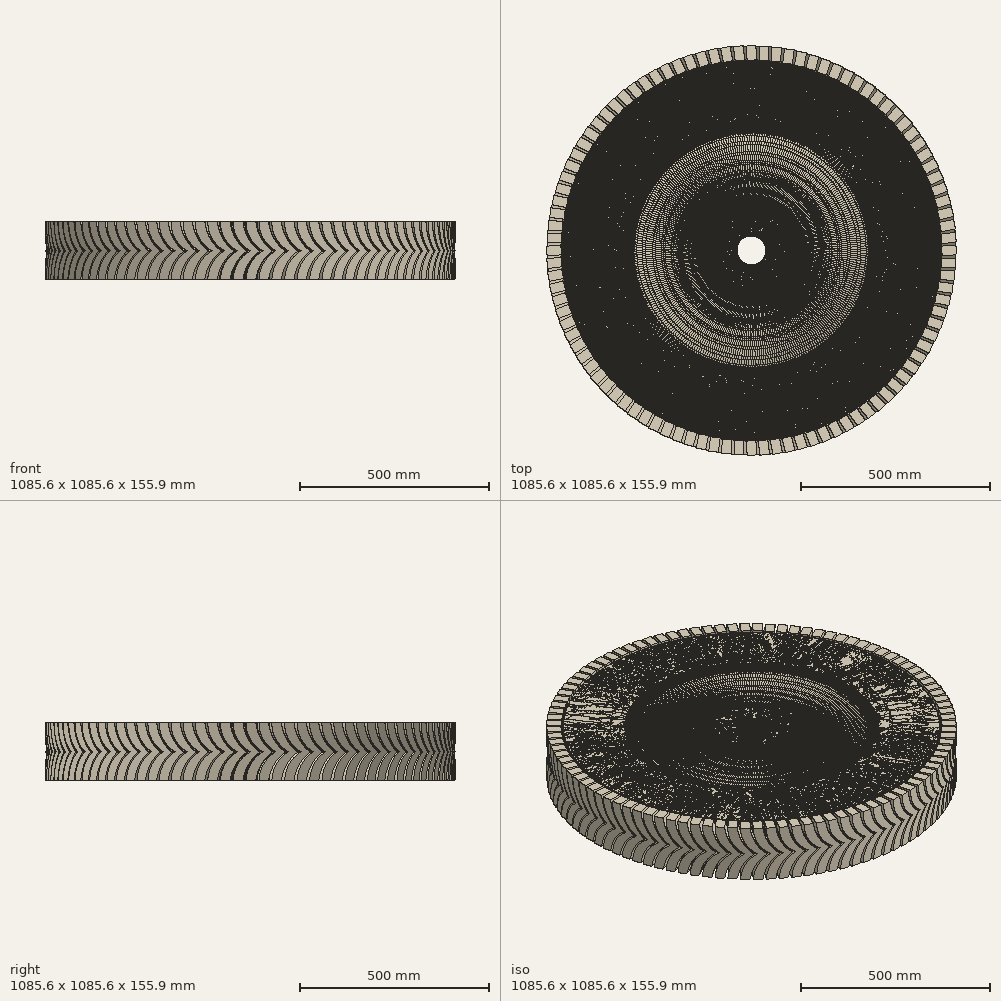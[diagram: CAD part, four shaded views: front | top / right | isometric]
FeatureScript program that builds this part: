
annotation { "Feature Type Name" : "Feature", "Feature Type Description" : "" }
export const myFeature = defineFeature(function(context is Context, id is Id, definition is map)
    precondition{}
    {
        {
            var Q0;
            Q0=qCreatedBy(makeId("Front.planeOp"),FACE);
            var sketch = newSketch(context, id + "F0", { "sketchPlane" : qUnion([Q0])});
            skLineSegment(sketch, "E0", {"start": v(0, 0) * mm, "end": v(0, -107.13) * mm, "construction": true});
            skLineSegment(sketch, "E1", {"start": v(0, 0) * mm, "end": v(0, 107.06) * mm, "construction": true});
            skLineSegment(sketch, "E2", {"start": v(0, 78.3) * mm, "end": v(0, -74.1) * mm});
            skLineSegment(sketch, "E3", {"start": v(0, -74.1) * mm, "end": v(101.6, -74.1) * mm});
            skLineSegment(sketch, "E4", {"start": v(0, 78.3) * mm, "end": v(101.6, 78.3) * mm});
            skLineSegment(sketch, "E5", {"start": v(0, 0) * mm, "end": v(373.98, 0) * mm, "construction": true});
            skArc(sketch, "E6", {"start": v(101.6, 78.3) * mm, "mid": v(218.74, 49.67) * mm, "end": v(335.88, 78.3) * mm});
            skArc(sketch, "E7", {"start": v(335.88, -74.1) * mm, "mid": v(218.74, -45.48) * mm, "end": v(101.6, -74.1) * mm});
            skLineSegment(sketch, "E8", {"start": v(335.88, 78.3) * mm, "end": v(373.98, 78.3) * mm});
            skLineSegment(sketch, "E9", {"start": v(373.98, 78.3) * mm, "end": v(373.98, 65.6) * mm});
            skLineSegment(sketch, "E10", {"start": v(373.98, 65.6) * mm, "end": v(348.58, 65.6) * mm});
            skLineSegment(sketch, "E11", {"start": v(335.88, -74.1) * mm, "end": v(373.98, -74.1) * mm});
            skLineSegment(sketch, "E12", {"start": v(373.98, -74.1) * mm, "end": v(373.98, -61.4) * mm});
            skLineSegment(sketch, "E13", {"start": v(373.98, -61.4) * mm, "end": v(348.58, -61.4) * mm});
            skLineSegment(sketch, "E14", {"start": v(348.58, 65.6) * mm, "end": v(348.58, -61.4) * mm});
            skSolve(sketch);
        }
        {
            var Q0;
            Q0=makeQuery(id+"F0.imprint","IMPRINT",FACE,{"disambiguationData":[TD([[makeQuery(id+"F0.imprint","IMPRINT",EDGE,{"derivedFrom":sQuery(id+"F0.wireOp",EDGE,"E2")}),1.0]])]});
            var Q1;
            Q1=sQuery(id+"F0.wireOp",EDGE,"E1");
            revolve(context, id + "F1", {"entities" : qUnion([Q0]), "axis" : qUnion([Q1]), "revolveType" : RevolveType.FULL});
        }
        {
            var Q0;
            Q0=qCreatedBy(makeId("Top.planeOp"),FACE);
            var sketch = newSketch(context, id + "F2", { "sketchPlane" : qUnion([Q0])});
            skArc(sketch, "E15", {"start": v(-132.61, -265.07) * mm, "mid": v(136.67, -263) * mm, "end": v(293.13, -43.83) * mm});
            skLineSegment(sketch, "E16", {"start": v(0, 0) * mm, "end": v(491.38, -8.3) * mm, "construction": true});
            skArc(sketch, "E17", {"start": v(293.13, -43.83) * mm, "mid": v(196.1, -23.66) * mm, "end": v(97.19, -29.53) * mm});
            skArc(sketch, "E18.2.0", {"start": v(-29.3, -97.26) * mm, "mid": v(-86.9, -177.5) * mm, "end": v(-132.61, -265.07) * mm});
            skArc(sketch, "E19.1.0", {"start": v(98.87, 23.26) * mm, "mid": v(197.17, 13.5) * mm, "end": v(295.86, 17.69) * mm});
            skArc(sketch, "E19.1.1", {"start": v(-108.6, 275.77) * mm, "mid": v(-77.56, 181.67) * mm, "end": v(-23.02, 98.93) * mm});
            skArc(sketch, "E19.2.0", {"start": v(-69.58, 74) * mm, "mid": v(-110.27, 164) * mm, "end": v(-163.25, 247.38) * mm});
            skArc(sketch, "E19.2.1", {"start": v(-184.52, -231.94) * mm, "mid": v(-118.55, -158) * mm, "end": v(-74.16, -69.4) * mm});
            skArc(sketch, "E20.trimOffspring", {"start": v(-69.58, 74) * mm, "mid": v(-101.52, 3.24) * mm, "end": v(-74.16, -69.4) * mm});
            skArc(sketch, "E21.trimOffspring", {"start": v(-163.25, 247.38) * mm, "mid": v(-296.1, 13.14) * mm, "end": v(-184.52, -231.94) * mm});
            skArc(sketch, "E22.trimOffspring", {"start": v(98.87, 23.26) * mm, "mid": v(53.57, 86.3) * mm, "end": v(-23.02, 98.93) * mm});
            skArc(sketch, "E23.trimOffspring", {"start": v(295.86, 17.69) * mm, "mid": v(159.43, 249.86) * mm, "end": v(-108.6, 275.77) * mm});
            skArc(sketch, "E24", {"start": v(-29.3, -97.26) * mm, "mid": v(47.84, -89.33) * mm, "end": v(97.19, -29.53) * mm});
            skSolve(sketch);
        }
        {
            var Q0;
            Q0 = qSketchRegion(id + "F2", true);
            extrude(context, id + "F3", {"entities" : qUnion([Q0]), "operationType" : NewBodyOperationType.REMOVE, "endBound" : BoundingType.SYMMETRIC, "oppositeDirection" : true, "depth" : 553.72 * mm});
        }
        {
            var Q0;
            Q0=qCreatedBy(makeId("Top.planeOp"),FACE);
            var sketch = newSketch(context, id + "F4", { "sketchPlane" : qUnion([Q0])});
            skCircle(sketch, "E25", {"center": v(0, 0) * mm, "radius": 38.1 * mm});
            skCircle(sketch, "E26", {"center": v(11.35, 73) * mm, "radius": 19.05 * mm});
            skCircle(sketch, "E27.1.0", {"center": v(-68.89, -26.67) * mm, "radius": 19.05 * mm});
            skCircle(sketch, "E27.2.0", {"center": v(57.54, -46.32) * mm, "radius": 19.05 * mm});
            skSolve(sketch);
        }
        {
            var Q0;
            Q0 = qSketchRegion(id + "F4", true);
            extrude(context, id + "F5", {"entities" : qUnion([Q0]), "operationType" : NewBodyOperationType.REMOVE, "endBound" : BoundingType.SYMMETRIC, "oppositeDirection" : true, "depth" : 297.18 * mm});
        }
        {
            var Q0;
            Q0=qCreatedBy(makeId("Right.planeOp"),FACE);
            var sketch = newSketch(context, id + "F6", { "sketchPlane" : qUnion([Q0])});
            skLineSegment(sketch, "E28", {"start": v(373.96, 78.12) * mm, "end": v(373.96, 65.66) * mm});
            skLineSegment(sketch, "E29", {"start": v(373.96, 65.66) * mm, "end": v(348.2, 65.66) * mm});
            skLineSegment(sketch, "E30", {"start": v(348.2, 65.66) * mm, "end": v(348.2, -61.12) * mm});
            skLineSegment(sketch, "E31", {"start": v(348.2, -61.12) * mm, "end": v(373.96, -61.12) * mm});
            skLineSegment(sketch, "E32", {"start": v(373.96, -61.12) * mm, "end": v(373.94, -74.74) * mm});
            skLineSegment(sketch, "E33", {"start": v(373.94, -74.74) * mm, "end": v(498.1, -74.93) * mm});
            skLineSegment(sketch, "E34", {"start": v(498.1, 78.12) * mm, "end": v(373.96, 78.12) * mm});
            skLineSegment(sketch, "E35", {"start": v(0, 223.2) * mm, "end": v(0, -202.7) * mm, "construction": true});
            skArc(sketch, "E36", {"start": v(498.1, -74.93) * mm, "mid": v(512.88, 1.6) * mm, "end": v(498.1, 78.12) * mm});
            skSolve(sketch);
        }
        {
            var Q0;
            Q0 = qSketchRegion(id + "F6", true);
            var Q1;
            Q1=sQuery(id+"F6.wireOp",EDGE,"E35");
            revolve(context, id + "F7", {"operationType" : NewBodyOperationType.ADD, "entities" : qUnion([Q0]), "axis" : qUnion([Q1]), "revolveType" : RevolveType.FULL});
        }
        {
            var Q0;
            Q0=qCreatedBy(makeId("Right.planeOp"),FACE);
            cPlane(context, id + "F8", {"entities" : qUnion([Q0]), "cplaneType" : CPlaneType.OFFSET, "offset" : 502.92 * mm, "width" : 152.4 * mm, "height" : 152.4 * mm});
        }
        {
            var Q0;
            Q0=qCreatedBy(id+"F8.planeOp",FACE);
            var sketch = newSketch(context, id + "F9", { "sketchPlane" : qUnion([Q0])});
            skLineSegment(sketch, "E37", {"start": v(0, 257.12) * mm, "end": v(0, -308.52) * mm, "construction": true});
            skLineSegment(sketch, "E38", {"start": v(-102.43, 79.58) * mm, "end": v(157.06, 79.58) * mm, "construction": true});
            skLineSegment(sketch, "E39", {"start": v(-99.02, -76.34) * mm, "end": v(171.85, -76.34) * mm, "construction": true});
            skArc(sketch, "E40", {"start": v(0, 0) * mm, "mid": v(-32.76, -32.2) * mm, "end": v(-45.52, -76.34) * mm});
            skArc(sketch, "E41", {"start": v(-45.52, 79.58) * mm, "mid": v(-34.41, 33.12) * mm, "end": v(0, 0) * mm});
            skLineSegment(sketch, "E42", {"start": v(-45.52, 79.58) * mm, "end": v(-20.05, 79.58) * mm});
            skLineSegment(sketch, "E43", {"start": v(-45.52, -76.34) * mm, "end": v(-20.03, -76.34) * mm});
            skLineSegment(sketch, "E44", {"start": v(0, 0) * mm, "end": v(25.52, 0) * mm, "construction": true});
            skArc(sketch, "E45", {"start": v(25.52, 0) * mm, "mid": v(-5.16, -33.46) * mm, "end": v(-20.03, -76.34) * mm});
            skArc(sketch, "E46", {"start": v(-20.05, 79.58) * mm, "mid": v(-6, 34.8) * mm, "end": v(25.52, 0) * mm});
            skSolve(sketch);
        }
        {
            var Q0;
            Q0 = qSketchRegion(id + "F9", true);
            extrude(context, id + "F10", {"entities" : qUnion([Q0]), "operationType" : NewBodyOperationType.ADD, "depth" : 38.1 * mm});
        }
        {
            var Q0;
            Q0=makeQuery(id+"F1.opRevolve","SWEPT_BODY",BODY,{"disambiguationData":[OSD([sQuery(id+"F0.wireOp",EDGE,"E2"),sQuery(id+"F0.wireOp",EDGE,"E3"),sQuery(id+"F0.wireOp",EDGE,"E4"),sQuery(id+"F0.wireOp",EDGE,"E6"),sQuery(id+"F0.wireOp",EDGE,"E7"),sQuery(id+"F0.wireOp",EDGE,"E8"),sQuery(id+"F0.wireOp",EDGE,"E9"),sQuery(id+"F0.wireOp",EDGE,"E10"),sQuery(id+"F0.wireOp",EDGE,"E11"),sQuery(id+"F0.wireOp",EDGE,"E12"),sQuery(id+"F0.wireOp",EDGE,"E13"),sQuery(id+"F0.wireOp",EDGE,"E14")])]});
            var Q1;
            Q1=makeQuery(id+"F5.boolean.opBoolean","INTERSECT",EDGE,{"derivedFrom":[makeQuery(id+"F1.opRevolve","SWEPT_FACE",FACE,{"disambiguationData":[OSD([sQuery(id+"F0.wireOp",EDGE,"E4")])]}),makeQuery(id+"F5.opExtrude","SWEPT_FACE",FACE,{"disambiguationData":[OSD([sQuery(id+"F4.wireOp",EDGE,"E25")])]})]});
            circularPattern(context, id + "F11", {"entities" : qUnion([Q0]), "axis" : qUnion([Q1]), "angle" : 360 * degree, "instanceCount" : 100, "equalSpace" : true});
        }
    });
